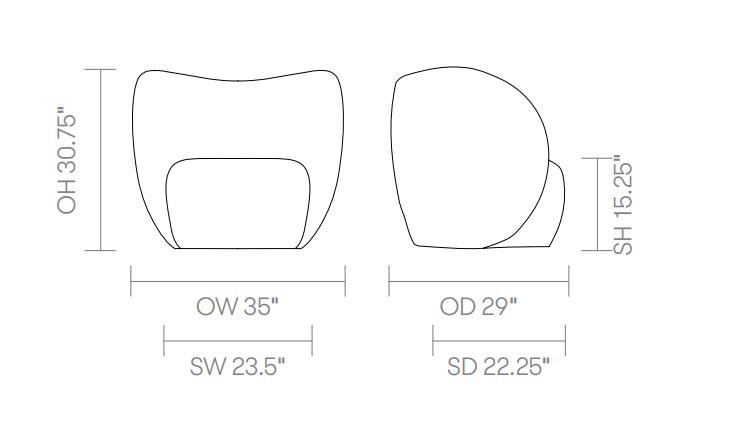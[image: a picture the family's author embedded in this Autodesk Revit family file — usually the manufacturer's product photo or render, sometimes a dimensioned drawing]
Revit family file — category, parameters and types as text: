
# Revit family: DBLTD_TheSenatorGroup_OfficeChairs_Bastille Lounge
name_source: partatom
category: Furniture
units: mm (PartAtom-declared; Revit-internal decimal feet)

## family parameters
Always vertical = Yes
Cut with Voids When Loaded = No
OmniClass Number = 23.40.20.00
OmniClass Title = General Furniture and Specialties
Render Appearance Source = Family Geometry
Room Calculation Point = No
Shared = Yes
Work Plane-Based = No

## types (3) — shared parameters
Assembly Code = E2020200
AssetType = Movable
Category = Pr_40_50_12_57 Office chairs
Color = Upholstery: Various.
Constituents = Frame, Seat and Back
DurationUnit = years
ExpectedLife = 5
Finish = Upholstery: Various.
Keynote = Pr_40_50_12_57 Office chairs
Manufacturer = The Senator Group
ManufacturerName = The Senator Group
ManufacturerURL = https://www.allermuir.com
Material = Moulded foam back rest, Cut foam seat carcass, Fully upholstered, Plastic glides
Name = Chair
ProductInformation = https://www.allermuir.com
SeatingHeight = 385 mm  [stored 1.26312 ft]
Shape = Rectangular
URL = https://www.thesenatorgroup.com
Uniclass2015Code = Pr_40_50_12_57
Uniclass2015Title = Office chairs
Uniclass2015Version = Products v1.15
Version = 1
WarrantyDescription = The Senator Group warrants that its manufactured products are free from manufacturing defects - in materials or workmanship - for a period of five (5) years.
WarrantyDurationLabor = 5
WarrantyDurationParts = 5
WarrantyDurationUnit = years
WarrantyGuarantorLabor = https://www.thesenatorgroup.com
WarrantyGuarantorParts = https://www.thesenatorgroup.com
zero-valued in all types: Cost, Default Elevation

## per-type parameters (varying)
| type | Model | ModelNumber | NominalDepth | NominalHeight | NominalWidth | SeatType | Size |
| 1 Seat Club Chair | BST100 | BST100 | 735 mm | 780 mm  [stored 2.55906 ft] | 890 mm  [stored 2.91995 ft] | Nestred_DBLTD_TheSenatorGroup_OfficeChairs_BastilleLounge_1 | 890 x 735 x 780 mm |
| 2 Seat Sofa | BST200 | BST200 | 835 mm | 790 mm  [stored 2.59186 ft] | 1810 mm  [stored 5.93832 ft] | Nestred_DBLTD_TheSenatorGroup_OfficeChairs_BastilleLounge_2 | 1810 x 835 x 790 mm |
| 3 Seat Sofa | BST300 | BST300 | 920 mm  [stored 3.01837 ft] | 790 mm  [stored 2.59186 ft] | 2440 mm  [stored 8.00525 ft] | Nestred_DBLTD_TheSenatorGroup_OfficeChairs_BastilleLounge_3 | 2440 x 920 x 790 mm |

note: column(s) folded — value = type name in every type: Description, ModelReference, Type Comments

note: [stored X ft] marks values corroborated as IEEE doubles in the binary element streams (Revit-internal decimal feet)

## geometry (parser evidence)
native form markers: Sweep x9
no freeform markers — native parametric forms only
